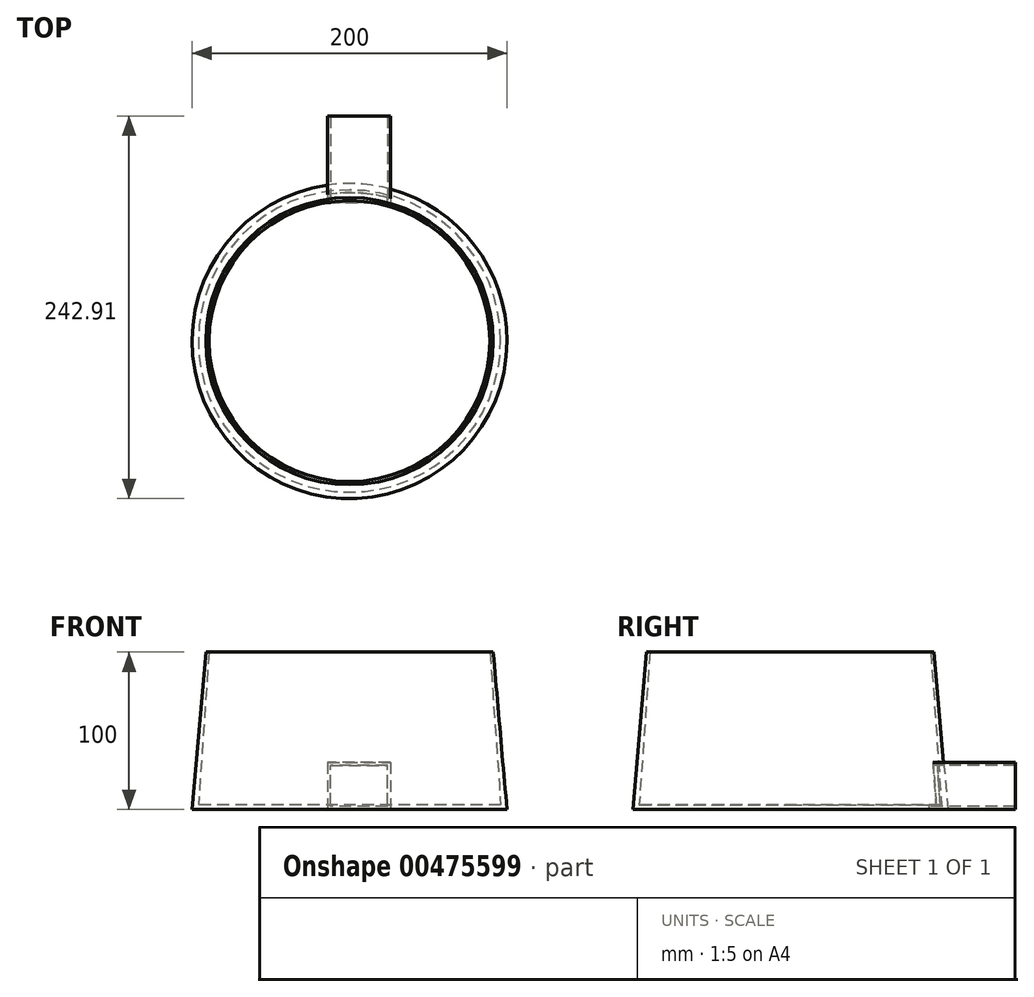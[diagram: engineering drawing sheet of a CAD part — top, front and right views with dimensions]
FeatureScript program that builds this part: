
annotation { "Feature Type Name" : "Feature", "Feature Type Description" : "" }
export const myFeature = defineFeature(function(context is Context, id is Id, definition is map)
    precondition{}
    {
        {
            var Q0;
            Q0=qCreatedBy(makeId("Top.planeOp"),FACE);
            var sketch = newSketch(context, id + "F0", { "sketchPlane" : qUnion([Q0])});
            skLineSegment(sketch, "E0.bottom", {"start": v(-13.04, 47.61) * mm, "end": v(26.96, 47.61) * mm});
            skLineSegment(sketch, "E0.top", {"start": v(-13.04, -7.39) * mm, "end": v(26.96, -7.39) * mm});
            skLineSegment(sketch, "E0.left", {"start": v(-13.04, 47.61) * mm, "end": v(-13.04, -7.39) * mm});
            skLineSegment(sketch, "E0.right", {"start": v(26.96, 47.61) * mm, "end": v(26.96, -7.39) * mm});
            skSolve(sketch);
        }
        {
            var Q0;
            Q0 = qSketchRegion(id + "F0", true);
            extrude(context, id + "F1", {"entities" : qUnion([Q0]), "depth" : 30 * mm});
        }
        {
            var Q0;
            Q0=makeQuery(id+"F1.opExtrude","SWEPT_FACE",FACE,{"disambiguationData":[OSD([sQuery(id+"F0.wireOp",EDGE,"E0.top")])]});
            var sketch = newSketch(context, id + "F2", { "sketchPlane" : qUnion([Q0])});
            skLineSegment(sketch, "E1.bottom", {"start": v(-11.04, 28) * mm, "end": v(24.96, 28) * mm});
            skLineSegment(sketch, "E1.top", {"start": v(-11.04, 2) * mm, "end": v(24.96, 2) * mm});
            skLineSegment(sketch, "E1.left", {"start": v(-11.04, 28) * mm, "end": v(-11.04, 2) * mm});
            skLineSegment(sketch, "E1.right", {"start": v(24.96, 28) * mm, "end": v(24.96, 2) * mm});
            skSolve(sketch);
        }
        {
            var Q0;
            Q0 = qSketchRegion(id + "F2", true);
            extrude(context, id + "F3", {"entities" : qUnion([Q0]), "operationType" : NewBodyOperationType.REMOVE, "oppositeDirection" : true, "depth" : 189.1 * mm, "hasSecondDirection" : true, "secondDirectionOppositeDirection" : false, "secondDirectionDepth" : 48.4 * mm});
        }
        {
            var Q0;
            Q0=qCreatedBy(makeId("Top.planeOp"),FACE);
            var sketch = newSketch(context, id + "F4", { "sketchPlane" : qUnion([Q0])});
            skCircle(sketch, "E2", {"center": v(0.86, -108.2) * mm, "radius": 100 * mm});
            skSolve(sketch);
        }
        {
            var Q0;
            Q0 = qSketchRegion(id + "F4", true);
            extrude(context, id + "F5", {"entities" : qUnion([Q0]), "operationType" : NewBodyOperationType.ADD, "depth" : 100 * mm, "hasDraft" : true, "draftAngle" : 5 * degree, "draftPullDirection" : true});
        }
        {
            var Q0;
            Q0=makeQuery(id+"F1.opExtrude","SWEPT_BODY",BODY,{"disambiguationData":[OSD([sQuery(id+"F0.wireOp",EDGE,"E0.bottom"),sQuery(id+"F0.wireOp",EDGE,"E0.top"),sQuery(id+"F0.wireOp",EDGE,"E0.left"),sQuery(id+"F0.wireOp",EDGE,"E0.right")])]});
            transform(context, id + "F6", {"entities" : qUnion([Q0]), "transformType" : TransformType.TRANSLATION_3D, "dx" : 0 * mm, "dy" : -12.9 * mm, "dz" : 0 * mm, "makeCopy" : false});
        }
        {
            var Q0;
            Q0=qCreatedBy(makeId("Top.planeOp"),FACE);
            cPlane(context, id + "F7", {"entities" : qUnion([Q0]), "cplaneType" : CPlaneType.OFFSET, "offset" : 3 * mm, "width" : 150 * mm, "height" : 150 * mm});
        }
        {
            var Q0;
            Q0=qCreatedBy(id+"F7.planeOp",FACE);
            var sketch = newSketch(context, id + "F8", { "sketchPlane" : qUnion([Q0])});
            skCircle(sketch, "E3", {"center": v(0.86, -108.2) * mm, "radius": 96 * mm});
            skSolve(sketch);
        }
        {
            var Q0;
            Q0 = qSketchRegion(id + "F8", true);
            extrude(context, id + "F9", {"entities" : qUnion([Q0]), "operationType" : NewBodyOperationType.REMOVE, "depth" : 100 * mm, "hasDraft" : true, "draftAngle" : 4 * degree, "draftPullDirection" : true});
        }
    });
